# Revit family: Sanitary_Toilet-Accessories_hansgrohe_41753XXX-AddStoris-Roll-holder-with-cove_
name_source: partatom
category: Plumbing Fixtures
revit_build: Autodesk Revit 2015 (Build: 20140322_1515(x64)
units: mm (PartAtom-declared; Revit-internal decimal feet)

## types (6) — shared parameters
BIMobject category = Toilet Accessories
BIMobject category code = sanitary-toilet-accessories
BIMobject main category = Sanitary
BIMobject main category code = sanitary
Brand url = http://www.hansgrohe-int.com
Design country = Germany
Edition number = 1
GTIN code = https://4059625297018
IFC Classification = Sanitary Terminal
Installation instructions = https://www.hansgrohe.com
Manufacturer country = Germany
Manufacturer name = hansgrohe
Material main = Metal
Product Guid = 6220aba7-d9dc-4a98-adfe-e30b90b4a916
Product SKU = 41753XXX
Product data url = https://bimobject.com
Product family = AddStoris
Product group = Roll holders
Product name = 41753XXX AddStoris Roll holder with cover
Product url = https://www.hansgrohe.com
QR code = http://bimobject.com
Technical description = https://www.hansgrohe.com

## type names (no varying parameters)
- 000 Chrome
- 140 Brushed Bronze
- 340 Brushed Black Chrome
- 670 Matte Black
- 700 Matt White
- 990 Polished Gold Optic

## geometry (parser evidence)
native form markers: Sweep x2
no freeform markers — native parametric forms only
